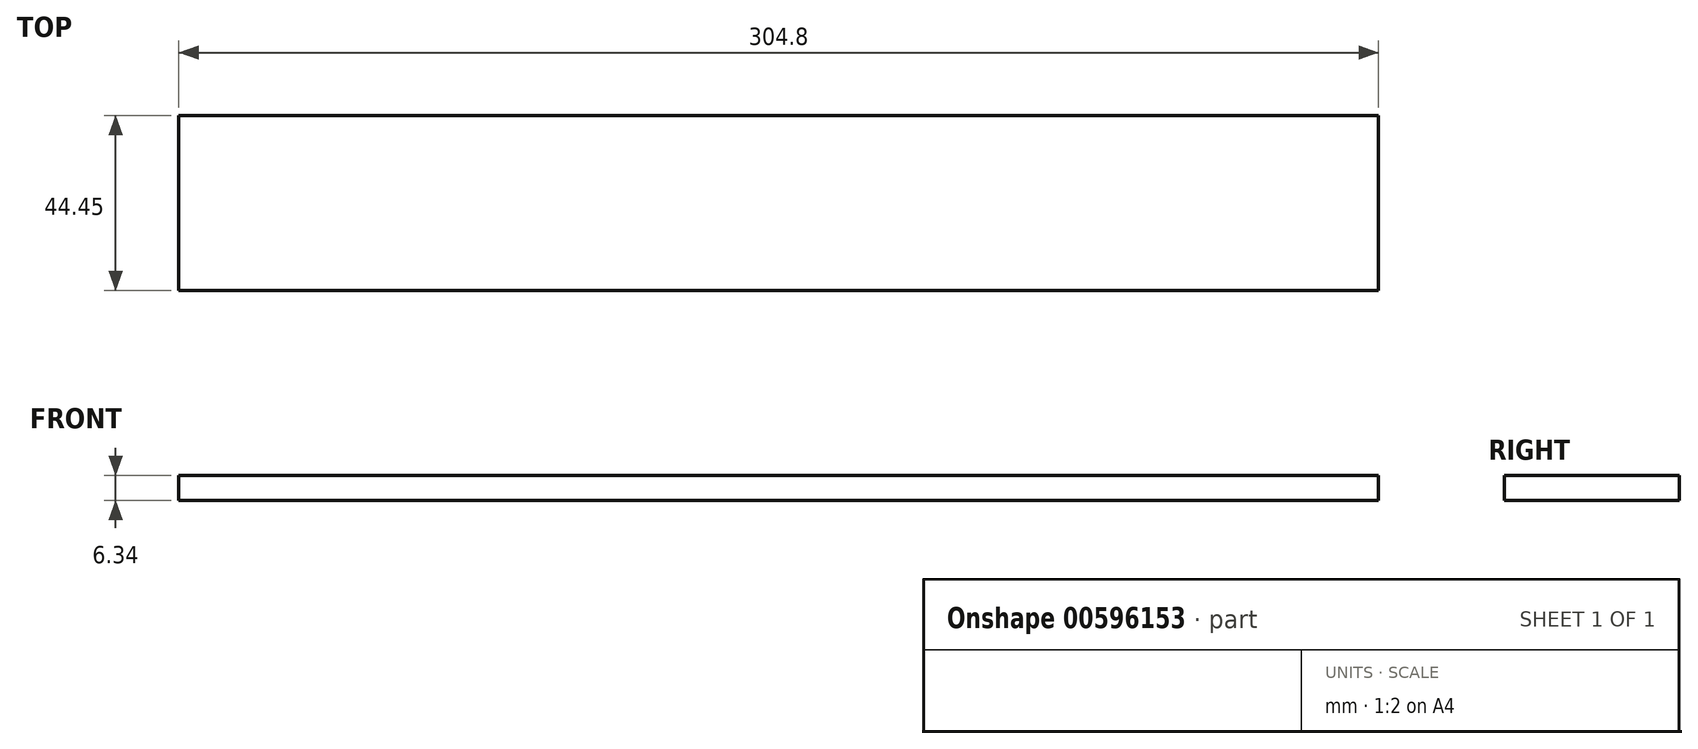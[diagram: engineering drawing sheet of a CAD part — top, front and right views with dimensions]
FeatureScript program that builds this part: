
annotation { "Feature Type Name" : "Feature", "Feature Type Description" : "" }
export const myFeature = defineFeature(function(context is Context, id is Id, definition is map)
    precondition{}
    {
        {
            var Q0;
            Q0=qCreatedBy(makeId("Front.planeOp"),FACE);
            var sketch = newSketch(context, id + "F0", { "sketchPlane" : qUnion([Q0])});
            skLineSegment(sketch, "E0.bottom", {"start": v(152.4, -3.17) * mm, "end": v(-152.4, -3.18) * mm});
            skLineSegment(sketch, "E0.top", {"start": v(152.4, 3.18) * mm, "end": v(-152.4, 3.17) * mm});
            skLineSegment(sketch, "E0.left", {"start": v(152.4, -3.17) * mm, "end": v(152.4, 3.18) * mm});
            skLineSegment(sketch, "E0.right", {"start": v(-152.4, -3.17) * mm, "end": v(-152.4, 3.18) * mm});
            skPoint(sketch, "E0.middle", {"position": v(0, 0) * mm});
            skSolve(sketch);
        }
        {
            var Q0;
            Q0=makeQuery(id+"F0.imprint","IMPRINT",FACE,{"disambiguationData":[TD([[makeQuery(id+"F0.imprint","IMPRINT",EDGE,{"derivedFrom":sQuery(id+"F0.wireOp",EDGE,"E0.bottom")}),-1.0]])]});
            extrude(context, id + "F1", {"entities" : qUnion([Q0]), "depth" : 44.45 * mm, "offsetDistance" : 25.4 * mm});
        }
    });
